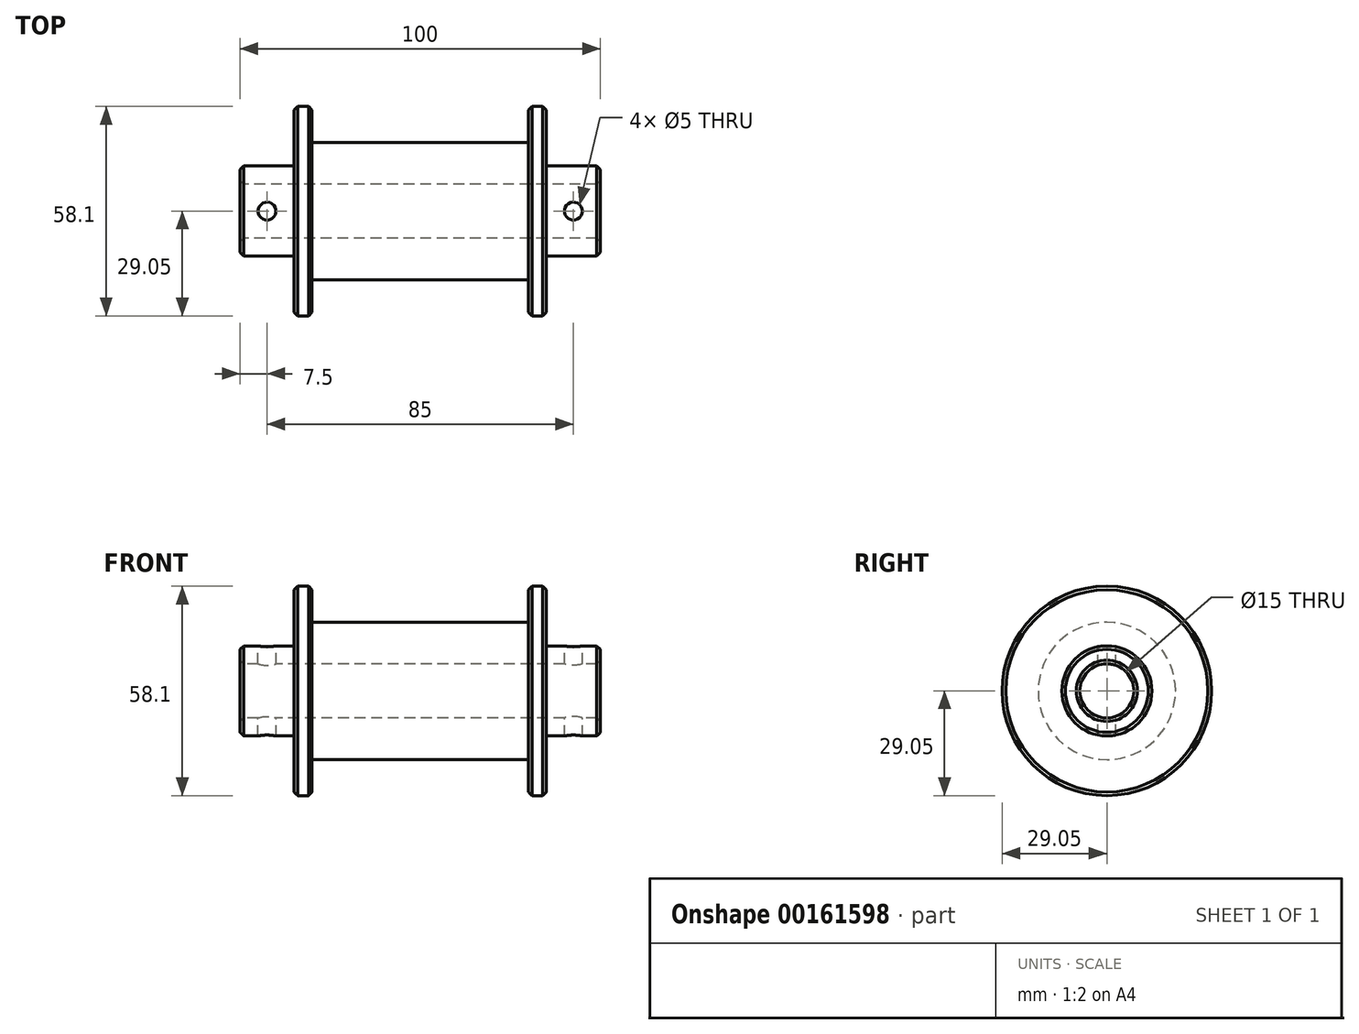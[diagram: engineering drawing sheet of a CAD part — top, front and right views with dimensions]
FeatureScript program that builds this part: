
annotation { "Feature Type Name" : "Feature", "Feature Type Description" : "" }
export const myFeature = defineFeature(function(context is Context, id is Id, definition is map)
    precondition{}
    {
        {
            var Q0;
            Q0=qCreatedBy(makeId("Right.planeOp"),FACE);
            var sketch = newSketch(context, id + "F0", { "sketchPlane" : qUnion([Q0])});
            skCircle(sketch, "E0", {"center": v(0, 0) * mm, "radius": 7.5 * mm});
            skCircle(sketch, "E1", {"center": v(0, 0) * mm, "radius": 19.05 * mm});
            skSolve(sketch);
        }
        {
            var Q0;
            Q0 = qSketchRegion(id + "F0", true);
            extrude(context, id + "F1", {"entities" : qUnion([Q0]), "endBound" : BoundingType.SYMMETRIC, "depth" : 60 * mm});
        }
        {
            var Q0;
            Q0=makeQuery(id+"F1.opExtrude","CAP_FACE",FACE,{"disambiguationData":[OSD([sQuery(id+"F0.wireOp",EDGE,"E0"),sQuery(id+"F0.wireOp",EDGE,"E1")])],"isStart":false});
            var sketch = newSketch(context, id + "F2", { "sketchPlane" : qUnion([Q0])});
            skCircle(sketch, "E2.0", {"center": v(0, 0) * mm, "radius": 29.05 * mm});
            skCircle(sketch, "E3.0", {"center": v(0, 0) * mm, "radius": 7.5 * mm});
            skSolve(sketch);
        }
        {
            var Q0;
            Q0 = qSketchRegion(id + "F2", true);
            extrude(context, id + "F3", {"entities" : qUnion([Q0]), "depth" : 5 * mm});
        }
        {
            var Q0;
            Q0=makeQuery(id+"F3.opExtrude","CAP_FACE",FACE,{"disambiguationData":[OSD([sQuery(id+"F2.wireOp",EDGE,"E2.0"),sQuery(id+"F2.wireOp",EDGE,"E3.0")])],"isStart":false});
            var sketch = newSketch(context, id + "F4", { "sketchPlane" : qUnion([Q0])});
            skCircle(sketch, "E4.0", {"center": v(0, 0) * mm, "radius": 7.5 * mm});
            skCircle(sketch, "E5.0", {"center": v(0, 0) * mm, "radius": 12.5 * mm});
            skSolve(sketch);
        }
        {
            var Q0;
            Q0 = qSketchRegion(id + "F4", true);
            extrude(context, id + "F5", {"entities" : qUnion([Q0]), "operationType" : NewBodyOperationType.ADD, "depth" : 15 * mm});
        }
        {
            var Q0;
            Q0=makeQuery(id+"F3.opExtrude","CAP_EDGE",EDGE,{"disambiguationData":[OSD([sQuery(id+"F2.wireOp",EDGE,"E2.0")])],"isStart":false});
            var Q1;
            Q1=makeQuery(id+"F3.opExtrude","CAP_EDGE",EDGE,{"disambiguationData":[OSD([sQuery(id+"F2.wireOp",EDGE,"E2.0")])],"isStart":true});
            var Q2;
            Q2=makeQuery(id+"F5.opExtrude","CAP_EDGE",EDGE,{"disambiguationData":[OSD([sQuery(id+"F4.wireOp",EDGE,"E5.0")])],"isStart":false});
            var Q3;
            Q3=makeQuery(id+"F5.opExtrude","CAP_EDGE",EDGE,{"disambiguationData":[OSD([sQuery(id+"F4.wireOp",EDGE,"E4.0")])],"isStart":false});
            chamfer(context, id + "F6", {"entities" : qUnion([Q0, Q1, Q2, Q3]), "width" : 1 * mm, "tangentPropagation" : true});
        }
        {
            var Q0;
            Q0=qCreatedBy(makeId("Top.planeOp"),FACE);
            var sketch = newSketch(context, id + "F7", { "sketchPlane" : qUnion([Q0])});
            skCircle(sketch, "E6", {"center": v(42.5, 0) * mm, "radius": 2.5 * mm});
            skLineSegment(sketch, "E7", {"start": v(50, 0) * mm, "end": v(35, 0) * mm, "construction": true});
            skSolve(sketch);
        }
        {
            var Q0;
            Q0 = qSketchRegion(id + "F7", true);
            extrude(context, id + "F8", {"entities" : qUnion([Q0]), "operationType" : NewBodyOperationType.REMOVE, "endBound" : BoundingType.SYMMETRIC, "oppositeDirection" : true, "depth" : 50 * mm});
        }
        {
            var Q0;
            Q0=makeQuery(id+"F3.opExtrude","SWEPT_BODY",BODY,{"disambiguationData":[OSD([sQuery(id+"F2.wireOp",EDGE,"E2.0"),sQuery(id+"F2.wireOp",EDGE,"E3.0")])]});
            var Q1;
            Q1=qCreatedBy(makeId("Right.planeOp"),FACE);
            mirror(context, id + "F9", {"operationType" : NewBodyOperationType.ADD, "entities" : qUnion([Q0]), "mirrorPlane" : qUnion([Q1])});
        }
    });
